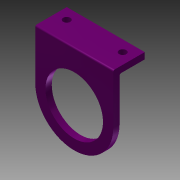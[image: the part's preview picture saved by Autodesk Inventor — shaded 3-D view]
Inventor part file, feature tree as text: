
AUTODESK INVENTOR PART (.ipt)
format: ipt  version: 2015 (Build 190159000, 159)  size: 115,200 bytes
history: native  units: mm
features: sketch x2, extrude x2, hole x1, pattern_linear x1, fillet x1
ambient origin geometry x8: Origin, YZ Plane, XZ Plane, XY Plane, X Axis, Y Axis, Z Axis, Center Point
bodies: Body1 (feature_tree)
feature tree (7):
  sketch  "Sketch1"  dims[d5=24.75mm d10=10.0mm]
  extrude  "Extrusion4"  Depth=10.0mm
  extrude  "Extrusion5"  Depth=24.75mm
  hole  "Hole2"  [1 undecoded]
  pattern_linear  "Rectangular Pattern2"  Spacing1=3.45mm  [1 undecoded]
  fillet  "Fillet1"  Radius=2.0mm
  sketch  "Sketch2"  dims[d28=18.25mm d29=24.75mm d30=24.75mm d31=3.45mm d34=2.0mm d35=0.0mm d36=2.0mm d37=0.0mm d38=3.5mm d39=3.5mm d40=2.25mm d41=6.0mm d42=4.0mm d43=2.0mm d44=90.0deg d45=8.0mm d46=20.594885mm d47=20.0mm d49=17.75mm d50=10.0mm d52=17.75mm d53=0.5mm]
note: 2 required parameter values undecoded (feature->parameter linkage not recoverable at this tier; creation-order binding heuristic only, values carry confidence <= 0.55)
